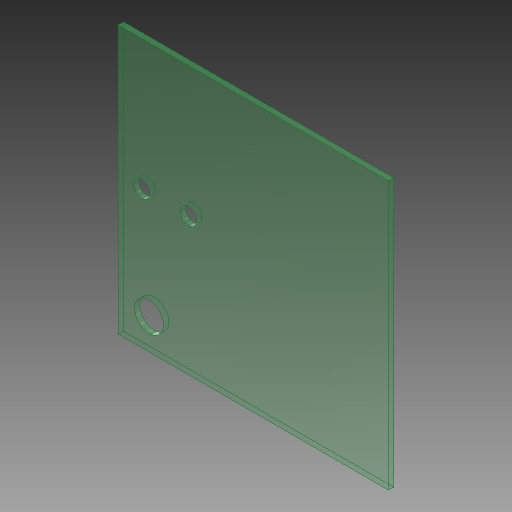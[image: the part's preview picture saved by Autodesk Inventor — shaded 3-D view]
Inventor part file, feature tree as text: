
AUTODESK INVENTOR PART (.ipt)
format: ipt  version: 2018.1 (Build 221171000, 171)  size: 122,368 bytes
history: native  units: mm
features: extrude x3, sketch x3
ambient origin geometry x8: Origin, YZ Plane, XZ Plane, XY Plane, X Axis, Y Axis, Z Axis, Center Point
bodies: Solid1 (feature_tree)
feature tree (6):
  extrude  "Extrusion1"  Depth=260.0mm
  extrude  "Extrusion3"  TaperAngle=0.0deg  [1 undecoded]
  extrude  "Extrusion4"  Depth=5.0mm
  sketch  "Sketch1"  dims[d0=258.0mm d1=260.0mm]
  sketch  "Sketch3"  dims[d2=5.0mm d3=0.0mm]
  sketch  "Sketch4"  dims[d12=29.5mm d13=29.5mm d14=28.0mm d15=5.0mm d16=0.0mm d17=25.0mm d18=22.5mm d19=132.5mm d20=16.0mm d21=25.0mm d22=45.0mm d23=16.0mm d24=132.5mm d25=5.0mm d26=0.0mm]
note: 1 required parameter value undecoded (feature->parameter linkage not recoverable at this tier; creation-order binding heuristic only, values carry confidence <= 0.55)
